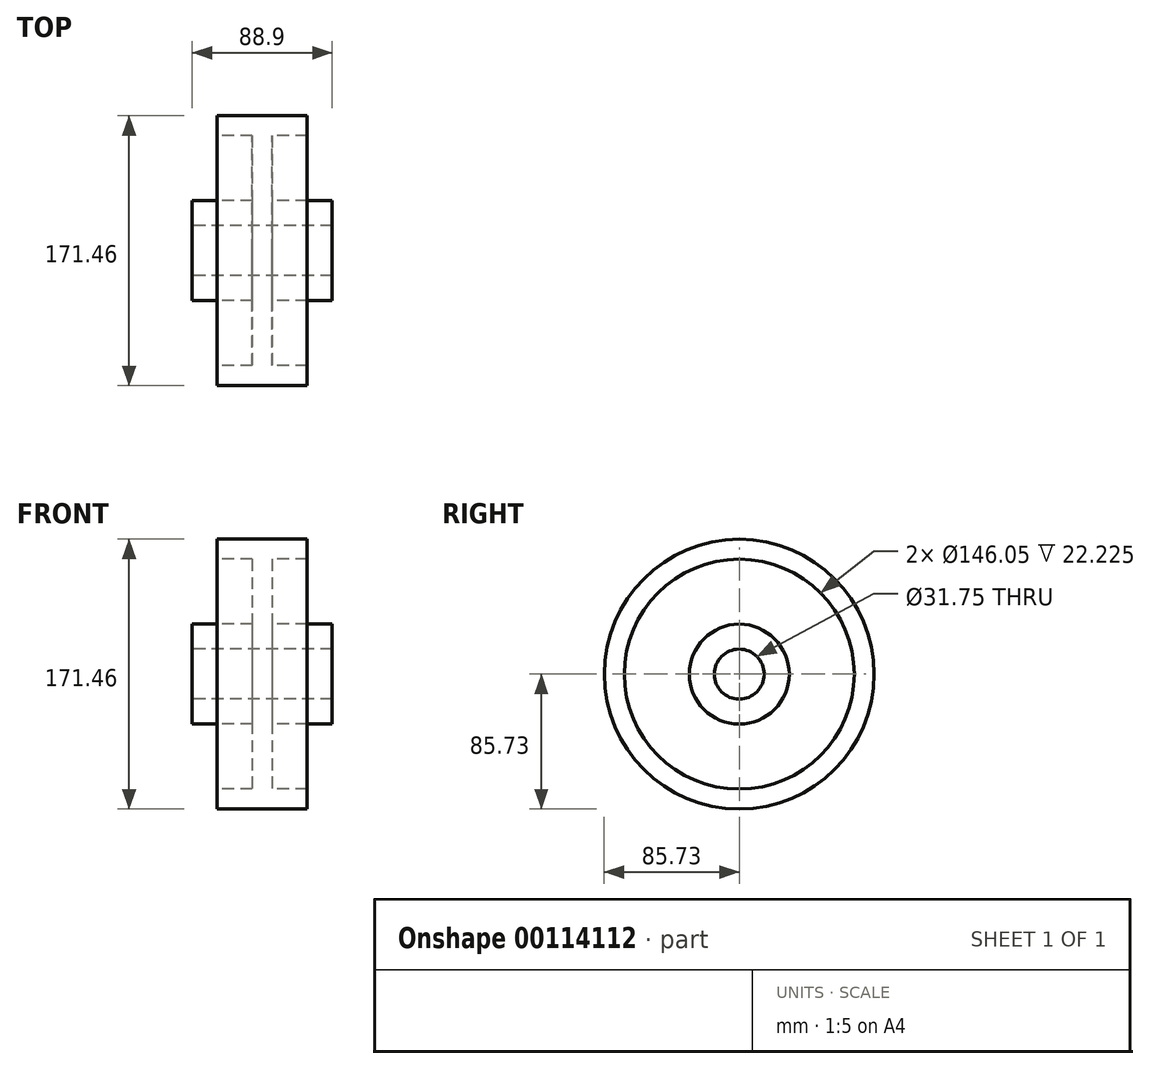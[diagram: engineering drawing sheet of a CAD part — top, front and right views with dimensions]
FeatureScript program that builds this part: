
annotation { "Feature Type Name" : "Feature", "Feature Type Description" : "" }
export const myFeature = defineFeature(function(context is Context, id is Id, definition is map)
    precondition{}
    {
        {
            var Q0;
            Q0=qCreatedBy(makeId("Front.planeOp"),FACE);
            var sketch = newSketch(context, id + "F0", { "sketchPlane" : qUnion([Q0])});
            skLineSegment(sketch, "E0", {"start": v(-245.23, 0) * mm, "end": v(259.43, 0) * mm, "construction": true});
            skLineSegment(sketch, "E1", {"start": v(0, 152.07) * mm, "end": v(0, -145.38) * mm, "construction": true});
            skLineSegment(sketch, "E2", {"start": v(-44.45, 15.87) * mm, "end": v(44.45, 15.87) * mm});
            skLineSegment(sketch, "E3", {"start": v(44.45, 15.87) * mm, "end": v(44.45, 31.75) * mm});
            skLineSegment(sketch, "E4", {"start": v(44.45, 31.75) * mm, "end": v(6.35, 31.75) * mm});
            skLineSegment(sketch, "E5", {"start": v(6.35, 31.75) * mm, "end": v(6.35, 73.02) * mm});
            skLineSegment(sketch, "E6", {"start": v(6.35, 73.02) * mm, "end": v(28.58, 73.02) * mm});
            skLineSegment(sketch, "E7", {"start": v(28.58, 73.03) * mm, "end": v(28.58, 85.73) * mm});
            skLineSegment(sketch, "E8", {"start": v(28.58, 85.73) * mm, "end": v(-28.57, 85.73) * mm});
            skLineSegment(sketch, "E9", {"start": v(-28.57, 85.73) * mm, "end": v(-28.57, 73.02) * mm});
            skLineSegment(sketch, "E10", {"start": v(-28.57, 73.02) * mm, "end": v(-6.35, 73.02) * mm});
            skLineSegment(sketch, "E11", {"start": v(-6.35, 73.02) * mm, "end": v(-6.35, 31.75) * mm});
            skLineSegment(sketch, "E12", {"start": v(-6.35, 31.75) * mm, "end": v(-44.45, 31.75) * mm});
            skLineSegment(sketch, "E13", {"start": v(-44.45, 31.75) * mm, "end": v(-44.45, 15.87) * mm});
            skSolve(sketch);
        }
        {
            var Q0;
            Q0=makeQuery(id+"F0.imprint","IMPRINT",FACE,{"disambiguationData":[TD([[makeQuery(id+"F0.imprint","IMPRINT",EDGE,{"derivedFrom":sQuery(id+"F0.wireOp",EDGE,"E2")}),1.0]])]});
            var Q1;
            Q1=sQuery(id+"F0.wireOp",EDGE,"E0");
            revolve(context, id + "F1", {"entities" : qUnion([Q0]), "axis" : qUnion([Q1]), "revolveType" : RevolveType.FULL});
        }
    });
